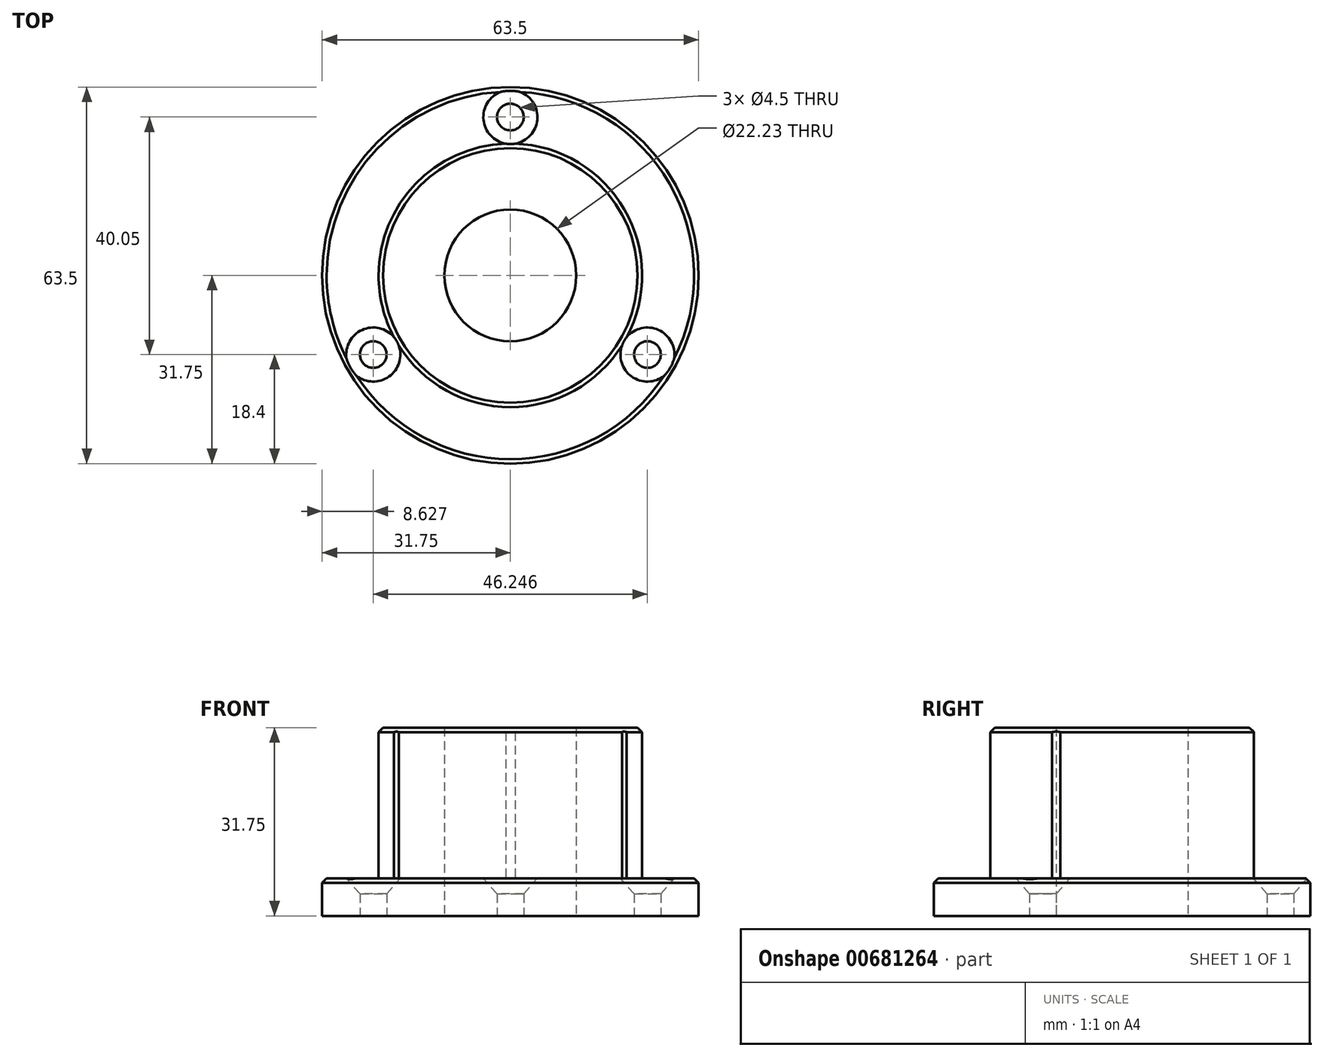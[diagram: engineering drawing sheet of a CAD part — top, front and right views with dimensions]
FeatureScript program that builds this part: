
annotation { "Feature Type Name" : "Feature", "Feature Type Description" : "" }
export const myFeature = defineFeature(function(context is Context, id is Id, definition is map)
    precondition{}
    {
        {
            var Q0;
            Q0=qCreatedBy(makeId("Front.planeOp"),FACE);
            var sketch = newSketch(context, id + "F0", { "sketchPlane" : qUnion([Q0])});
            skLineSegment(sketch, "E0", {"start": v(0, 31.75) * mm, "end": v(-22.23, 31.75) * mm});
            skLineSegment(sketch, "E1", {"start": v(-22.23, 31.75) * mm, "end": v(-22.22, 6.35) * mm});
            skLineSegment(sketch, "E2", {"start": v(-22.22, 6.35) * mm, "end": v(-31.75, 6.35) * mm});
            skLineSegment(sketch, "E3", {"start": v(-31.75, 6.35) * mm, "end": v(-31.75, 0) * mm});
            skLineSegment(sketch, "E4", {"start": v(-31.75, 0) * mm, "end": v(0, 0) * mm});
            skLineSegment(sketch, "E5", {"start": v(0, 0) * mm, "end": v(0, 31.75) * mm});
            skSolve(sketch);
        }
        {
            var Q0;
            Q0=makeQuery(id+"F0.imprint","IMPRINT",FACE,{"disambiguationData":[TD([[makeQuery(id+"F0.imprint","IMPRINT",EDGE,{"derivedFrom":sQuery(id+"F0.wireOp",EDGE,"E0")}),1.0]])]});
            var Q1;
            Q1=sQuery(id+"F0.wireOp",EDGE,"E5");
            revolve(context, id + "F1", {"entities" : qUnion([Q0]), "axis" : qUnion([Q1]), "revolveType" : RevolveType.FULL});
        }
        {
            var Q0;
            Q0=makeQuery(id+"F1.opRevolve","SWEPT_FACE",FACE,{"disambiguationData":[OSD([sQuery(id+"F0.wireOp",EDGE,"E0")])]});
            var sketch = newSketch(context, id + "F2", { "sketchPlane" : qUnion([Q0])});
            skPoint(sketch, "E6", {"position": v(0, 0) * mm});
            skSolve(sketch);
        }
        {
            var Q0;
            Q0=sQuery(id+"F2.wireOp",VERTEX,"E6");
            var Q1;
            Q1=makeQuery(id+"F1.opRevolve","SWEPT_BODY",BODY,{"disambiguationData":[OSD([sQuery(id+"F0.wireOp",EDGE,"E0"),sQuery(id+"F0.wireOp",EDGE,"E1"),sQuery(id+"F0.wireOp",EDGE,"E2"),sQuery(id+"F0.wireOp",EDGE,"E3"),sQuery(id+"F0.wireOp",EDGE,"E4"),sQuery(id+"F0.wireOp",EDGE,"E5")])]});
            hole(context, id + "F3", {"style" : HoleStyle.SIMPLE, "endStyle" : HoleEndStyle.THROUGH, "holeDiameter" : 22.22 * mm, "majorDiameter" : 6.35 * mm, "isTappedThrough" : true, "tappedDepth" : 20.65 * mm, "tapClearance" : 3, "locations" : qUnion([Q0]), "scope" : qUnion([Q1]), "startStyle" : HoleStartStyle.PART});
        }
        {
            var Q0;
            Q0=makeQuery(id+"F1.opRevolve","SWEPT_FACE",FACE,{"disambiguationData":[OSD([sQuery(id+"F0.wireOp",EDGE,"E2")])]});
            var sketch = newSketch(context, id + "F4", { "sketchPlane" : qUnion([Q0])});
            skCircle(sketch, "E7", {"center": v(0, 26.7) * mm, "radius": 2.36 * mm});
            skCircle(sketch, "E8.1.0", {"center": v(-23.12, -13.35) * mm, "radius": 2.36 * mm});
            skCircle(sketch, "E8.2.0", {"center": v(23.12, -13.35) * mm, "radius": 2.36 * mm});
            skPoint(sketch, "E8.center", {"position": v(0, 0) * mm});
            skSolve(sketch);
        }
        {
            var Q0;
            Q0=sQuery(id+"F4.wireOp",VERTEX,"E7.center");
            var Q1;
            Q1=sQuery(id+"F4.wireOp",VERTEX,"E8.1.0.center");
            var Q2;
            Q2=sQuery(id+"F4.wireOp",VERTEX,"E8.2.0.center");
            var Q3;
            Q3=makeQuery(id+"F1.opRevolve","SWEPT_BODY",BODY,{"disambiguationData":[OSD([sQuery(id+"F0.wireOp",EDGE,"E0"),sQuery(id+"F0.wireOp",EDGE,"E1"),sQuery(id+"F0.wireOp",EDGE,"E2"),sQuery(id+"F0.wireOp",EDGE,"E3"),sQuery(id+"F0.wireOp",EDGE,"E4"),sQuery(id+"F0.wireOp",EDGE,"E5")])]});
            hole(context, id + "F5", {"style" : HoleStyle.C_SINK, "endStyle" : HoleEndStyle.THROUGH, "standardTappedOrClearance" : lookupTablePath({ "standard" : "ANSI", "fit" : "Normal (ASME)", "size" : "#8", "type" : "Clearance" }), "standardBlindInLast" : lookupTablePath({ "fit" : "Free", "standard" : "ANSI", "size" : "#8", "type" : "Clearance" }), "holeDiameter" : 4.5 * mm, "cSinkDiameter" : 9.12 * mm, "cSinkAngle" : 82 * degree, "majorDiameter" : 6.35 * mm, "isTappedThrough" : true, "tappedDepth" : 20.65 * mm, "tapClearance" : 3, "locations" : qUnion([Q0, Q1, Q2]), "scope" : qUnion([Q3]), "startStyle" : HoleStartStyle.PART});
        }
        {
            var Q0;
            Q0=makeQuery(id+"F1.opRevolve","SWEPT_EDGE",EDGE,{"disambiguationData":[OSD([sQuery(id+"F0.wireOp",EDGE,"E0"),sQuery(id+"F0.wireOp",EDGE,"E1")])]});
            var Q1;
            Q1=makeQuery(id+"F1.opRevolve","SWEPT_EDGE",EDGE,{"disambiguationData":[OSD([sQuery(id+"F0.wireOp",EDGE,"E2"),sQuery(id+"F0.wireOp",EDGE,"E3")])]});
            chamfer(context, id + "F6", {"entities" : qUnion([Q0, Q1]), "width" : 0.76 * mm, "tangentPropagation" : true});
        }
    });
